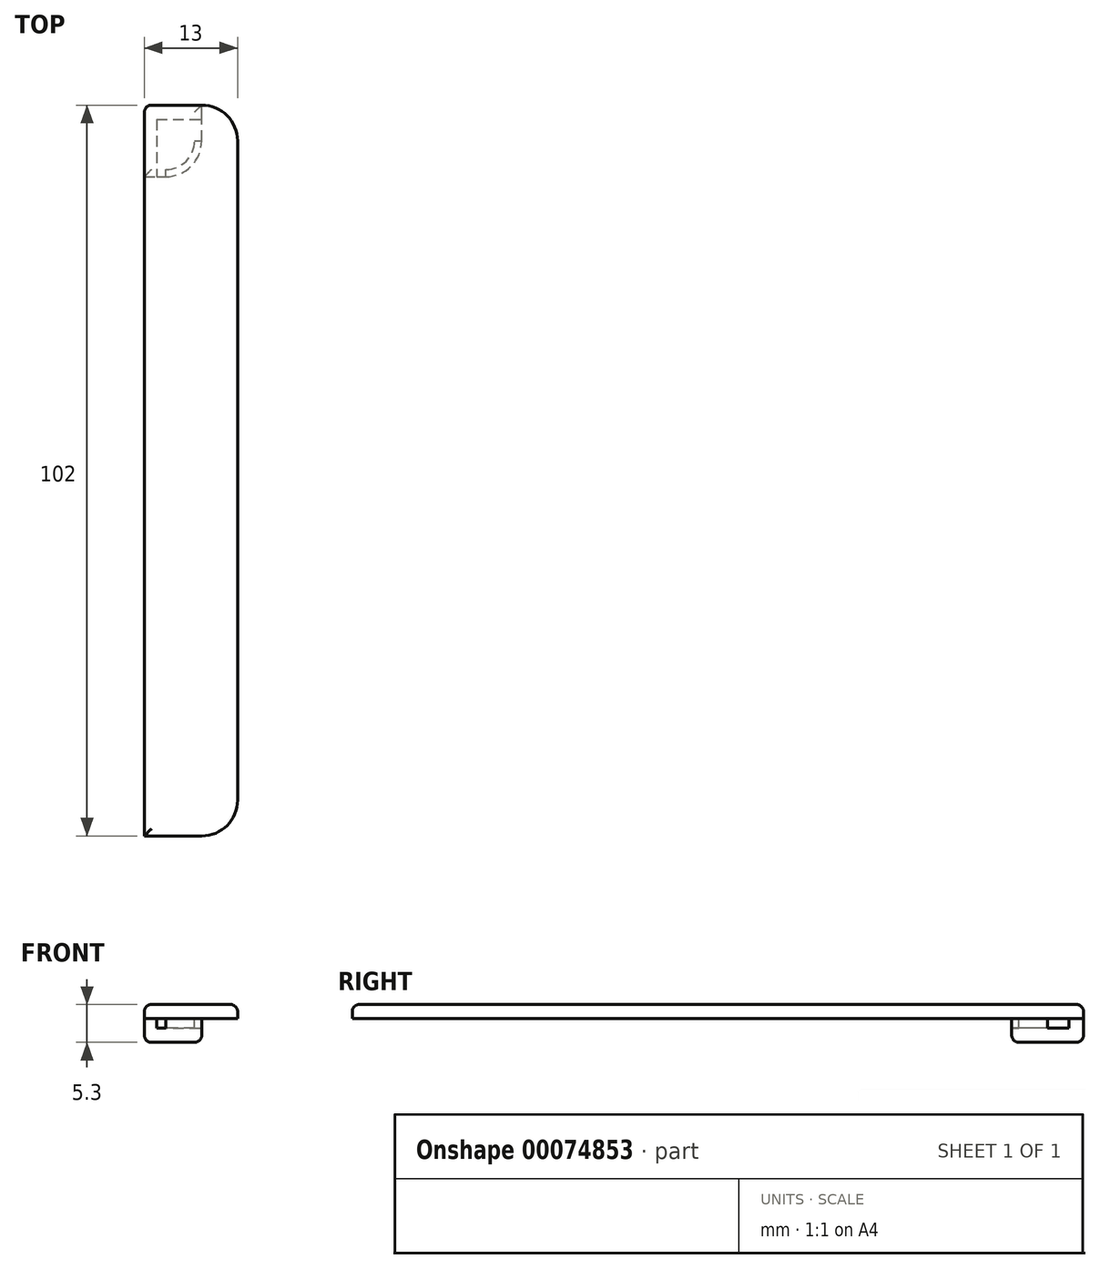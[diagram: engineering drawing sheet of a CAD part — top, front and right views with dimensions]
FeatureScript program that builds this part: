
annotation { "Feature Type Name" : "Feature", "Feature Type Description" : "" }
export const myFeature = defineFeature(function(context is Context, id is Id, definition is map)
    precondition{}
    {
        {
            var Q0;
            Q0=qCreatedBy(makeId("Top.planeOp"),FACE);
            var sketch = newSketch(context, id + "F0", { "sketchPlane" : qUnion([Q0])});
            skLineSegment(sketch, "E0.bottom", {"start": v(6.5, -51) * mm, "end": v(-6.5, -51) * mm});
            skLineSegment(sketch, "E0.top", {"start": v(1.5, 51) * mm, "end": v(-6.5, 51) * mm});
            skLineSegment(sketch, "E0.left", {"start": v(6.5, -51) * mm, "end": v(6.5, 46) * mm});
            skLineSegment(sketch, "E0.right", {"start": v(-6.5, -51) * mm, "end": v(-6.5, 51) * mm});
            skPoint(sketch, "E0.middle", {"position": v(0, 0) * mm});
            skPoint(sketch, "E1.visualSharp", {"position": v(6.5, 51) * mm});
            skArc(sketch, "E1.filletArc", {"start": v(6.5, 46) * mm, "mid": v(5.04, 49.54) * mm, "end": v(1.5, 51) * mm});
            skSolve(sketch);
        }
        {
            var Q0;
            Q0=qSketchRegion(id+"F0",true);
            extrude(context, id + "F1", {"entities" : qUnion([Q0]), "depth" : 2 * mm});
        }
        {
            var Q0;
            Q0=makeQuery(id+"F1.opExtrude","CAP_FACE",FACE,{"disambiguationData":[OSD([sQuery(id+"F0.wireOp",EDGE,"E0.bottom"),sQuery(id+"F0.wireOp",EDGE,"E0.top"),sQuery(id+"F0.wireOp",EDGE,"E0.left"),sQuery(id+"F0.wireOp",EDGE,"E0.right"),sQuery(id+"F0.wireOp",EDGE,"E1.filletArc")])],"isStart":true});
            var sketch = newSketch(context, id + "F2", { "sketchPlane" : qUnion([Q0])});
            skLineSegment(sketch, "E2.bottom", {"start": v(-6.5, -51) * mm, "end": v(1.5, -51) * mm});
            skLineSegment(sketch, "E2.top", {"start": v(-6.5, -49) * mm, "end": v(1.5, -49) * mm});
            skLineSegment(sketch, "E2.left", {"start": v(-6.5, -49) * mm, "end": v(-6.5, -51) * mm});
            skLineSegment(sketch, "E2.right", {"start": v(1.5, -49) * mm, "end": v(1.5, -51) * mm});
            skLineSegment(sketch, "E3.bottom", {"start": v(-6.5, -51) * mm, "end": v(-4.8, -51) * mm});
            skLineSegment(sketch, "E3.top", {"start": v(-6.5, -41) * mm, "end": v(-4.8, -41) * mm});
            skLineSegment(sketch, "E3.left", {"start": v(-6.5, -51) * mm, "end": v(-6.5, -41) * mm});
            skLineSegment(sketch, "E3.right", {"start": v(-4.8, -51) * mm, "end": v(-4.8, -41) * mm});
            skSolve(sketch);
        }
        {
            var Q0;
            Q0=qSketchRegion(id+"F2",true);
            extrude(context, id + "F3", {"entities" : qUnion([Q0]), "operationType" : NewBodyOperationType.ADD, "depth" : 1.3 * mm});
        }
        {
            var Q0;
            Q0=makeQuery(id+"F3.opExtrude","CAP_FACE",FACE,{"disambiguationData":[OSD([sQuery(id+"F2.wireOp",EDGE,"E2.bottom"),sQuery(id+"F2.wireOp",EDGE,"E2.top"),sQuery(id+"F2.wireOp",EDGE,"E2.right"),sQuery(id+"F2.wireOp",EDGE,"E3.bottom"),sQuery(id+"F2.wireOp",EDGE,"E3.top"),sQuery(id+"F2.wireOp",EDGE,"E3.left"),sQuery(id+"F2.wireOp",EDGE,"E3.right")])],"isStart":false});
            var sketch = newSketch(context, id + "F4", { "sketchPlane" : qUnion([Q0])});
            skLineSegment(sketch, "E4.bottom", {"start": v(1.5, -51) * mm, "end": v(-6.5, -51) * mm});
            skLineSegment(sketch, "E4.top", {"start": v(1.5, -41) * mm, "end": v(-6.5, -41) * mm});
            skLineSegment(sketch, "E4.left", {"start": v(1.5, -51) * mm, "end": v(1.5, -41) * mm});
            skLineSegment(sketch, "E4.right", {"start": v(-6.5, -51) * mm, "end": v(-6.5, -41) * mm});
            skSolve(sketch);
        }
        {
            var Q0;
            Q0=qSketchRegion(id+"F4",true);
            extrude(context, id + "F5", {"entities" : qUnion([Q0]), "operationType" : NewBodyOperationType.ADD, "depth" : 2 * mm});
        }
        {
            var Q0;
            Q0=makeQuery(id+"F1.opExtrude","SWEPT_EDGE",EDGE,{"disambiguationData":[OSD([sQuery(id+"F0.wireOp",EDGE,"E0.bottom"),sQuery(id+"F0.wireOp",EDGE,"E0.left")])]});
            var Q1;
            Q1=makeQuery(id+"F5.opExtrude","SWEPT_EDGE",EDGE,{"disambiguationData":[OSD([sQuery(id+"F4.wireOp",EDGE,"E4.top"),sQuery(id+"F4.wireOp",EDGE,"E4.left")])]});
            fillet(context, id + "F6", {"entities" : qUnion([Q0, Q1]), "radius" : 5 * mm, "tangentPropagation" : true, "allowEdgeOverflow" : false});
        }
        {
            var Q0;
            Q0=makeQuery(id+"F1.opExtrude","CAP_FACE",FACE,{"disambiguationData":[OSD([sQuery(id+"F0.wireOp",EDGE,"E0.bottom"),sQuery(id+"F0.wireOp",EDGE,"E0.top"),sQuery(id+"F0.wireOp",EDGE,"E0.left"),sQuery(id+"F0.wireOp",EDGE,"E0.right"),sQuery(id+"F0.wireOp",EDGE,"E1.filletArc")])],"isStart":false});
            fillet(context, id + "F7", {"entities" : qUnion([Q0]), "radius" : 1 * mm, "tangentPropagation" : true, "allowEdgeOverflow" : false});
        }
        {
            var Q0;
            Q0=makeQuery(id+"F5.boolean.opBoolean","MERGE",EDGE,{"derivedFrom":[makeQuery(id+"F3.boolean.opBoolean","MERGE",EDGE,{"derivedFrom":[makeQuery(id+"F1.opExtrude","SWEPT_EDGE",EDGE,{"disambiguationData":[OSD([sQuery(id+"F0.wireOp",EDGE,"E0.top"),sQuery(id+"F0.wireOp",EDGE,"E0.right")])]}),makeQuery(id+"F3.opExtrude","SWEPT_EDGE",EDGE,{"disambiguationData":[OSD([sQuery(id+"F2.wireOp",EDGE,"E3.bottom"),sQuery(id+"F2.wireOp",EDGE,"E3.left")])]})]}),makeQuery(id+"F5.opExtrude","SWEPT_EDGE",EDGE,{"disambiguationData":[OSD([sQuery(id+"F4.wireOp",EDGE,"E4.bottom"),sQuery(id+"F4.wireOp",EDGE,"E4.right")])]})]});
            var Q1;
            Q1=makeQuery(id+"F5.opExtrude","CAP_FACE",FACE,{"disambiguationData":[OSD([sQuery(id+"F4.wireOp",EDGE,"E4.bottom"),sQuery(id+"F4.wireOp",EDGE,"E4.top"),sQuery(id+"F4.wireOp",EDGE,"E4.left"),sQuery(id+"F4.wireOp",EDGE,"E4.right")])],"isStart":false});
            fillet(context, id + "F8", {"entities" : qUnion([Q0, Q1]), "radius" : 1 * mm, "tangentPropagation" : true, "allowEdgeOverflow" : false});
        }
        {
            var Q0;
            Q0=makeQuery(id+"F1.opExtrude","CAP_FACE",FACE,{"disambiguationData":[OSD([sQuery(id+"F0.wireOp",EDGE,"E0.bottom"),sQuery(id+"F0.wireOp",EDGE,"E0.top"),sQuery(id+"F0.wireOp",EDGE,"E0.left"),sQuery(id+"F0.wireOp",EDGE,"E0.right"),sQuery(id+"F0.wireOp",EDGE,"E1.filletArc")])],"isStart":true});
            var sketch = newSketch(context, id + "F9", { "sketchPlane" : qUnion([Q0])});
            skLineSegment(sketch, "E5.0.0", {"start": v(0.5, -46) * mm, "end": v(1.5, -46) * mm});
            skArc(sketch, "E5.0.1", {"start": v(-3.5, -41) * mm, "mid": v(0.04, -42.46) * mm, "end": v(1.5, -46) * mm});
            skLineSegment(sketch, "E5.0.2", {"start": v(-3.5, -41) * mm, "end": v(-3.5, -42) * mm});
            skArc(sketch, "E5.0.3", {"start": v(-3.5, -42) * mm, "mid": v(-0.67, -43.17) * mm, "end": v(0.5, -46) * mm});
            skSolve(sketch);
        }
        {
            var Q0;
            Q0=qSketchRegion(id+"F9",true);
            extrude(context, id + "F10", {"entities" : qUnion([Q0]), "operationType" : NewBodyOperationType.ADD, "endBound" : BoundingType.UP_TO_NEXT, "depth" : 25 * mm});
        }
    });
